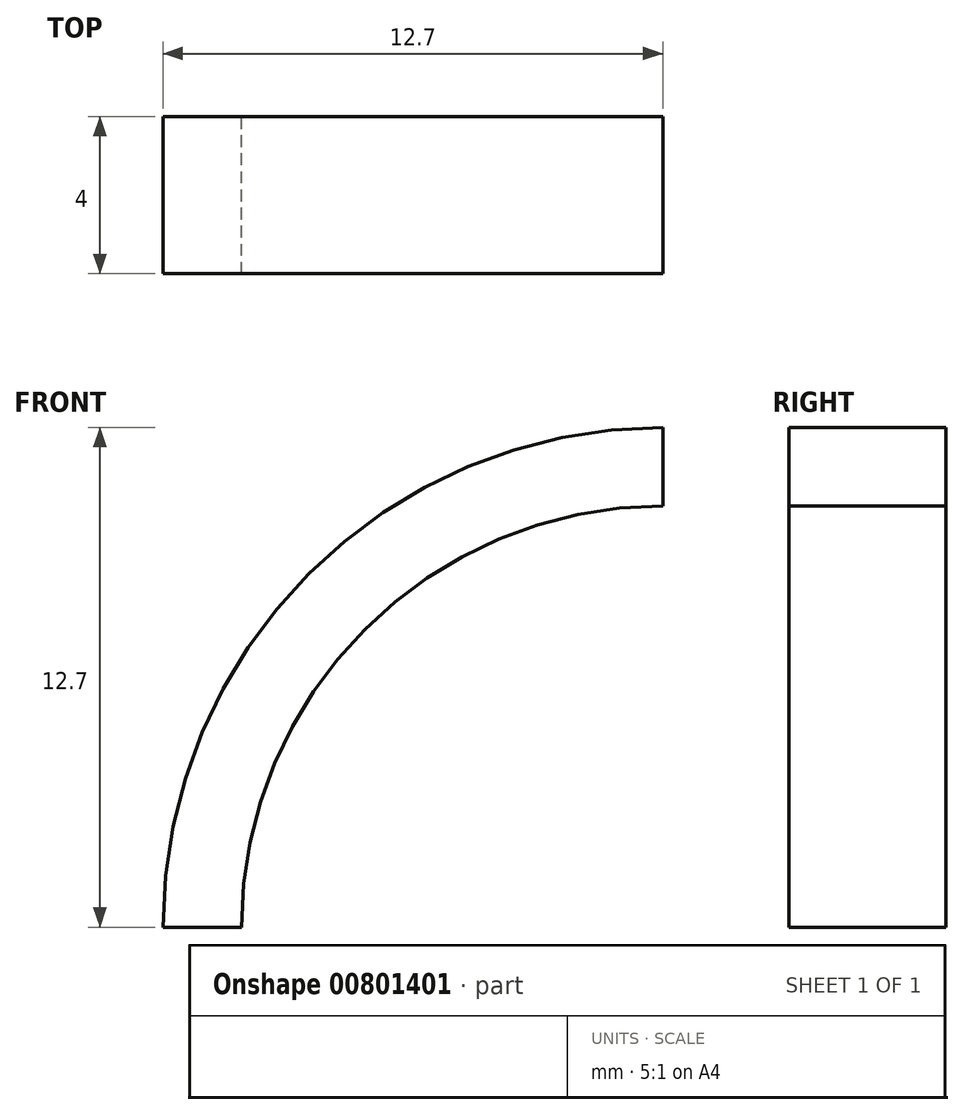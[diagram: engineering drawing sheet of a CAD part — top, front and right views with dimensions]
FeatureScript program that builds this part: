
annotation { "Feature Type Name" : "Feature", "Feature Type Description" : "" }
export const myFeature = defineFeature(function(context is Context, id is Id, definition is map)
    precondition{}
    {
        {
            var Q0;
            Q0=qCreatedBy(makeId("Front.planeOp"),FACE);
            var sketch = newSketch(context, id + "F0", { "sketchPlane" : qUnion([Q0])});
            skArc(sketch, "E0", {"start": v(0, 12.7) * mm, "mid": v(-8.98, 8.98) * mm, "end": v(-12.7, 0) * mm});
            skArc(sketch, "E1", {"start": v(0, 10.7) * mm, "mid": v(-7.57, 7.57) * mm, "end": v(-10.7, 0) * mm});
            skLineSegment(sketch, "E2", {"start": v(0, 12.7) * mm, "end": v(0, 10.7) * mm});
            skLineSegment(sketch, "E3", {"start": v(-10.7, 0) * mm, "end": v(-12.7, 0) * mm});
            skSolve(sketch);
        }
        {
            var Q0;
            Q0=qSketchRegion(id+"F0",true);
            extrude(context, id + "F1", {"entities" : qUnion([Q0]), "depth" : 2 * mm, "offsetDistance" : 25 * mm, "hasSecondDirection" : true, "secondDirectionOppositeDirection" : true, "secondDirectionDepth" : 2 * mm});
        }
    });
